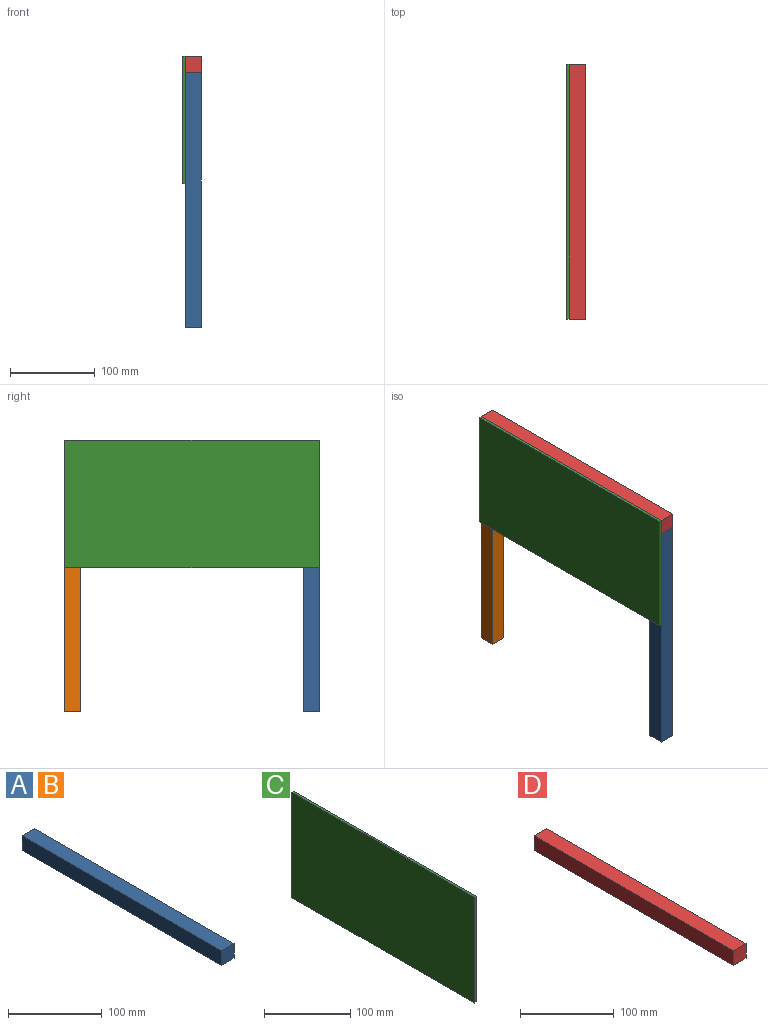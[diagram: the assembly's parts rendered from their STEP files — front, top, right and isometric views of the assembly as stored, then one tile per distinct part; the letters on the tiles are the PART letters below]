
ASSEMBLY  parts=4 mates=5
PART A: 6 faces, bbox 19x300x19 mm
  f0: plane 300x19mm, normal (0,0,1), area 5700mm2, adj f1,f3,f4,f5
  f1: plane 19x19mm, normal (0,-1,0), area 361mm2, adj f0,f2,f4,f5
  f2: plane 300x19mm, normal (0,0,-1), area 5700mm2, adj f1,f3,f4,f5
  f3: plane 19x19mm, normal (0,1,0), area 361mm2, adj f0,f2,f4,f5
  f4: plane 300x19mm, normal (1,0,0), area 5700mm2, adj f0,f1,f2,f3
  f5: plane 300x19mm, normal (-1,0,0), area 5700mm2, adj f0,f1,f2,f3
PART B: same geometry as A
PART C: 6 faces, bbox 3x300x150 mm
  f0: plane 300x3mm, normal (0,0,1), area 900mm2, adj f1,f3,f4,f5
  f1: plane 150x3mm, normal (0,-1,0), area 450mm2, adj f0,f2,f4,f5
  f2: plane 300x3mm, normal (0,0,-1), area 900mm2, adj f1,f3,f4,f5
  f3: plane 150x3mm, normal (0,1,0), area 450mm2, adj f0,f2,f4,f5
  f4: plane 300x150mm, normal (1,0,0), area 45000mm2, adj f0,f1,f2,f3
  f5: plane 300x150mm, normal (-1,0,0), area 45000mm2, adj f0,f1,f2,f3
PART D: 6 faces, bbox 19x300x19 mm
  f0: plane 300x19mm, normal (0,0,1), area 5700mm2, adj f1,f3,f4,f5
  f1: plane 300x19mm, normal (-1,0,0), area 5700mm2, adj f0,f2,f4,f5
  f2: plane 300x19mm, normal (0,0,-1), area 5700mm2, adj f1,f3,f4,f5
  f3: plane 300x19mm, normal (1,0,0), area 5700mm2, adj f0,f2,f4,f5
  f4: plane 19x19mm, normal (0,-1,0), area 361mm2, adj f0,f1,f2,f3
  f5: plane 19x19mm, normal (0,1,0), area 361mm2, adj f0,f1,f2,f3
PLACE A rot(axis=(-1,0,0),90deg) t=(-33.29,-176.25,-89.12)mm
PLACE B rot(axis=(0.58,-0.58,-0.58),120deg) t=(-23.79,114.25,-89.12)mm
PLACE C t=(-36.29,-35.75,4.88)mm
PLACE D rot(axis=(1,0,0),180deg) t=(-23.79,-185.75,70.38)mm
MATE parallel A.f1 <-> D.f0  axis (0,0,1) through (-33.29,-185.75,60.88)mm
MATE parallel B.f3 <-> C.f0  axis (0,0,1) through (-33.29,114.25,60.88)mm
MATE parallel A.f1 <-> C.f0  axis (0,0,1) through (-33.29,-185.75,60.88)mm
MATE parallel D.f1 <-> C.f4  axis (-1,0,0) through (-33.29,114.25,79.88)mm
MATE parallel B.f3 <-> D.f0  axis (0,0,1) through (-33.29,114.25,60.88)mm
